# Revit family: PRESTO ARTE-IE
name_source: partatom
category: Aparatos sanitarios
revit_build: Autodesk Revit 2015 (Build: 20140223_1515(x64)
units: mm (PartAtom-declared; Revit-internal decimal feet)

## types (1)
- 19700
    Accionamiento = Por pulsador
    CAUDAL = 1.2 L/Min
    Comentarios de tipo = ◦Llave de paso incorporada
◦Suministrado con tuerca y casquillo para tubo de Ø 28 mm
◦Con dispositivo antiSifónico que asegura la protección de la red de agua potable
◦contra las eventuales absorciones de agua contaminada
◦Cabeza intercambiable que comprende todo el mecanismo del fluxor interior
◦Pulsadores y tapa en acero inoxidable
◦Caja de empotrar y placa de fijación intermedia fabricadas con protección antioxidante
◦Sistema de Regulación para corregir distancias entre la caja de empotrar y la tapa en la instalación
◦Cuerpo del fluxor en latón niquelado con piezas interiores en materiales resistentes a la corrosión y a las incrustaciones calcáreas
◦Compatible con todos los bastidores de soporte Presto
◦Sistema de salida dirigida para reducir la sonoridad
◦Adaptable a espacios donde estaba instalado el fluxor 1000 A.
    Conexión AC = Sí
    Conexión AF = Sí
    Código de montaje = C1030220
    Descripción = Fluxor temporizado ecológico silencioso para encastrar en muro, cuerpo de latón niquelado y caja de empotrar con protección antioxidante. Dispositivo antiSifónico incorporado.
    ENTRADA = Macho 1"
    Elevación por defecto = 1219 mm
    Fabricante = PRESTO IBÉRICA
    Imagen de tipo = <Ninguno>
    Material = Persto Ibérica: ACERO INOXIDABLE
    Modelo = PRESTO ARTE IE
    PESO BRUTO = 2.520 Kg
    REFERENCIA = 19700
    Teléfono = (+34) 915 782 575
    URL = http://www.prestoiberica.com
